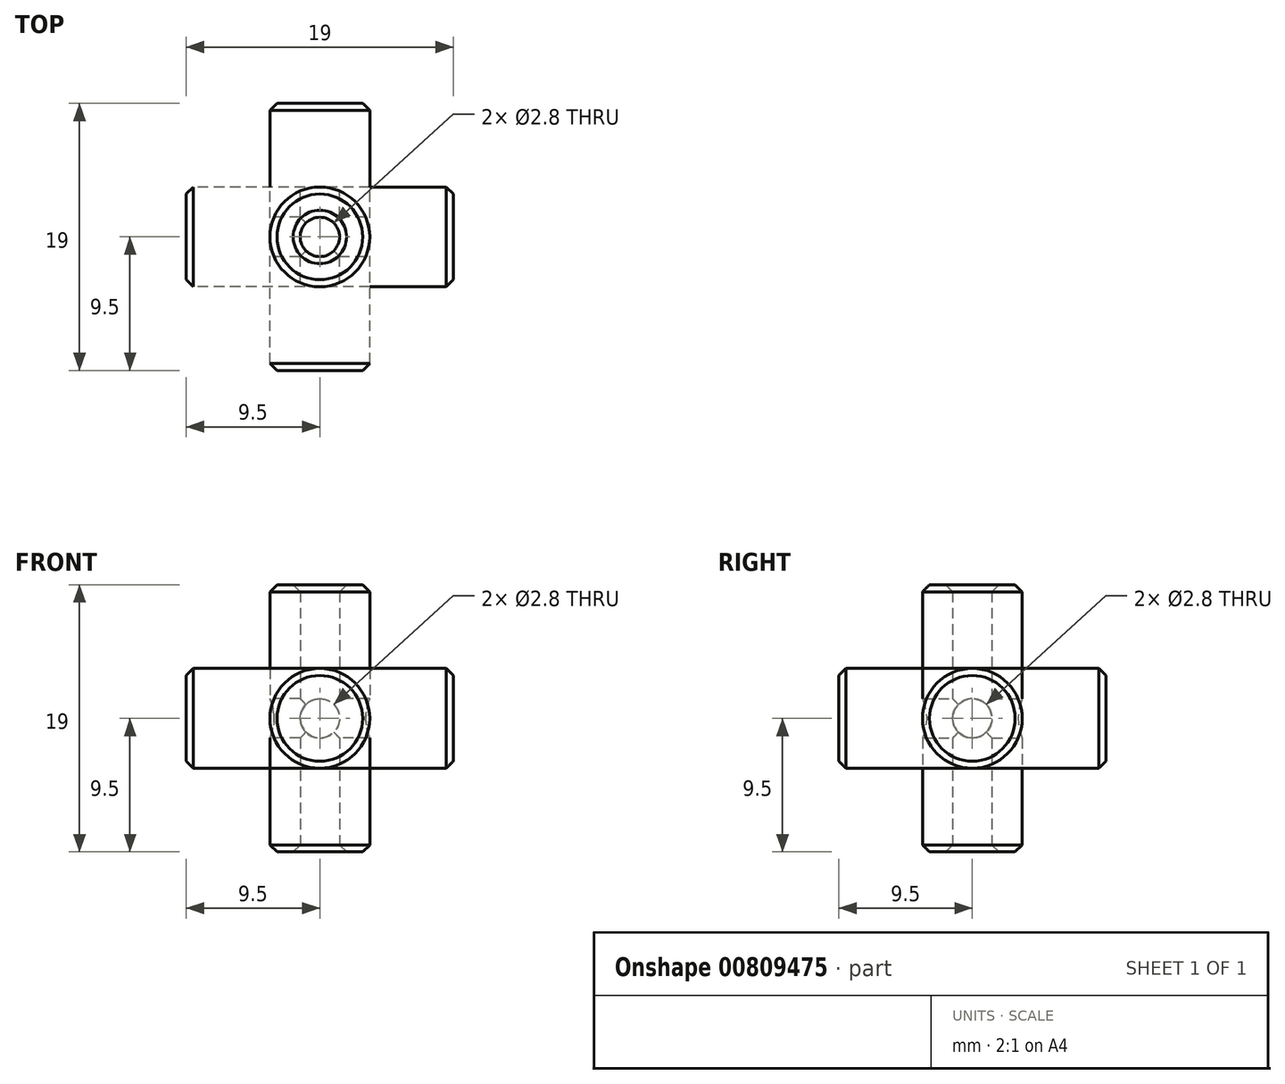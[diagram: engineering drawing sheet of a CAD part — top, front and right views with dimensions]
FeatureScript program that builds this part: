
annotation { "Feature Type Name" : "Feature", "Feature Type Description" : "" }
export const myFeature = defineFeature(function(context is Context, id is Id, definition is map)
    precondition{}
    {
        {
            var Q0;
            Q0=qCreatedBy(makeId("Front.planeOp"),FACE);
            var sketch = newSketch(context, id + "F0", { "sketchPlane" : qUnion([Q0])});
            skCircle(sketch, "E0", {"center": v(0, 0) * mm, "radius": 3.55 * mm});
            skSolve(sketch);
        }
        {
            var Q0;
            Q0=makeQuery(id+"F0.imprint","IMPRINT",FACE,{"disambiguationData":[TD([[makeQuery(id+"F0.imprint","IMPRINT",EDGE,{"derivedFrom":sQuery(id+"F0.wireOp",EDGE,"E0")}),1.0]])]});
            extrude(context, id + "F1", {"entities" : qUnion([Q0]), "endBound" : BoundingType.SYMMETRIC, "depth" : 19 * mm, "offsetDistance" : 25 * mm});
        }
        {
            var Q0;
            Q0=qCreatedBy(makeId("Front.planeOp"),FACE);
            var sketch = newSketch(context, id + "F2", { "sketchPlane" : qUnion([Q0])});
            skCircle(sketch, "E1", {"center": v(0, 0) * mm, "radius": 1.4 * mm});
            skSolve(sketch);
        }
        {
            var Q0;
            Q0 = qSketchRegion(id + "F2", true);
            extrude(context, id + "F3", {"entities" : qUnion([Q0]), "endBound" : BoundingType.SYMMETRIC, "depth" : 20 * mm, "offsetDistance" : 25 * mm});
        }
        {
            var Q0;
            Q0=qCreatedBy(makeId("Front.planeOp"),FACE);
            var sketch = newSketch(context, id + "F4", { "sketchPlane" : qUnion([Q0])});
            skLineSegment(sketch, "E2.bottom", {"start": v(0, 0) * mm, "end": v(10, 0) * mm});
            skLineSegment(sketch, "E2.top", {"start": v(0, 10) * mm, "end": v(10, 10) * mm});
            skLineSegment(sketch, "E2.left", {"start": v(0, 0) * mm, "end": v(0, 10) * mm});
            skLineSegment(sketch, "E2.right", {"start": v(10, 0) * mm, "end": v(10, 10) * mm});
            skSolve(sketch);
        }
        {
            var Q0;
            Q0 = qSketchRegion(id + "F4", true);
            extrude(context, id + "F5", {"entities" : qUnion([Q0]), "depth" : 10 * mm, "offsetDistance" : 25 * mm});
        }
        {
            var Q0;
            Q0=qCreatedBy(makeId("Origin.pointOp"),VERTEX);
            var Q1;
            Q1=makeQuery(id+"F5.opExtrude","CAP_VERTEX",VERTEX,{"disambiguationData":[OSD([sQuery(id+"F4.wireOp",EDGE,"E2.bottom"),sQuery(id+"F4.wireOp",EDGE,"E2.right")])],"isStart":false});
            var Q2;
            Q2=makeQuery(id+"F5.opExtrude","CAP_VERTEX",VERTEX,{"disambiguationData":[OSD([sQuery(id+"F4.wireOp",EDGE,"E2.top"),sQuery(id+"F4.wireOp",EDGE,"E2.right")])],"isStart":false});
            cPlane(context, id + "F6", {"entities" : qUnion([Q0, Q1, Q2]), "cplaneType" : CPlaneType.THREE_POINT, "offset" : 25 * mm, "width" : 150 * mm, "height" : 150 * mm});
        }
        {
            var Q0;
            Q0=qCreatedBy(id+"F6.planeOp",FACE);
            var sketch = newSketch(context, id + "F7", { "sketchPlane" : qUnion([Q0])});
            skLineSegment(sketch, "E3", {"start": v(0, 0) * mm, "end": v(-14.14, 10) * mm});
            skSolve(sketch);
        }
        {
            var Q0;
            Q0=makeQuery(id+"F5.opExtrude","SWEPT_BODY",BODY,{"disambiguationData":[OSD([sQuery(id+"F4.wireOp",EDGE,"E2.bottom"),sQuery(id+"F4.wireOp",EDGE,"E2.top"),sQuery(id+"F4.wireOp",EDGE,"E2.left"),sQuery(id+"F4.wireOp",EDGE,"E2.right")])]});
            deleteBodies(context, id + "F8", {"entities" : qUnion([Q0])});
        }
        {
            var Q0;
            Q0=makeQuery(id+"F3.opExtrude","SWEPT_BODY",BODY,{"disambiguationData":[OSD([sQuery(id+"F2.wireOp",EDGE,"E1")])]});
            var Q1;
            Q1=makeQuery(id+"F1.opExtrude","SWEPT_BODY",BODY,{"disambiguationData":[OSD([sQuery(id+"F0.wireOp",EDGE,"E0")])]});
            var Q2;
            Q2=sQuery(id+"F7.wireOp",EDGE,"E3");
            circularPattern(context, id + "F9", {"entities" : qUnion([Q0, Q1]), "axis" : qUnion([Q2]), "angle" : 360 * degree, "instanceCount" : 3, "equalSpace" : true});
        }
        {
            var Q0;
            Q0=makeQuery(id+"F9.opPattern","COPY",BODY,{"derivedFrom":makeQuery(id+"F3.opExtrude","SWEPT_BODY",BODY,{"disambiguationData":[OSD([sQuery(id+"F2.wireOp",EDGE,"E1")])]}),"instanceName":"2"});
            var Q1;
            Q1=makeQuery(id+"F9.opPattern","COPY",BODY,{"derivedFrom":makeQuery(id+"F3.opExtrude","SWEPT_BODY",BODY,{"disambiguationData":[OSD([sQuery(id+"F2.wireOp",EDGE,"E1")])]}),"instanceName":"1"});
            var Q2;
            Q2=makeQuery(id+"F3.opExtrude","SWEPT_BODY",BODY,{"disambiguationData":[OSD([sQuery(id+"F2.wireOp",EDGE,"E1")])]});
            var Q3;
            Q3=makeQuery(id+"F9.opPattern","COPY",BODY,{"derivedFrom":makeQuery(id+"F1.opExtrude","SWEPT_BODY",BODY,{"disambiguationData":[OSD([sQuery(id+"F0.wireOp",EDGE,"E0")])]}),"instanceName":"2"});
            booleanBodies(context, id + "F10", {"operationType" : BooleanOperationType.SUBTRACTION, "tools" : qUnion([Q0, Q1, Q2]), "targets" : qUnion([Q3])});
        }
        {
            var Q0;
            Q0=makeQuery(id+"F9.opPattern","COPY",FACE,{"derivedFrom":makeQuery(id+"F1.opExtrude","CAP_FACE",FACE,{"disambiguationData":[OSD([sQuery(id+"F0.wireOp",EDGE,"E0")])],"isStart":false}),"instanceName":"2"});
            var Q1;
            Q1=makeQuery(id+"F9.opPattern","COPY",FACE,{"derivedFrom":makeQuery(id+"F1.opExtrude","CAP_FACE",FACE,{"disambiguationData":[OSD([sQuery(id+"F0.wireOp",EDGE,"E0")])],"isStart":true}),"instanceName":"1"});
            var Q2;
            Q2=makeQuery(id+"F9.opPattern","COPY",FACE,{"derivedFrom":makeQuery(id+"F1.opExtrude","CAP_FACE",FACE,{"disambiguationData":[OSD([sQuery(id+"F0.wireOp",EDGE,"E0")])],"isStart":true}),"instanceName":"2"});
            var Q3;
            Q3=makeQuery(id+"F9.opPattern","COPY",FACE,{"derivedFrom":makeQuery(id+"F1.opExtrude","CAP_FACE",FACE,{"disambiguationData":[OSD([sQuery(id+"F0.wireOp",EDGE,"E0")])],"isStart":false}),"instanceName":"1"});
            var Q4;
            Q4=makeQuery(id+"F1.opExtrude","CAP_FACE",FACE,{"disambiguationData":[OSD([sQuery(id+"F0.wireOp",EDGE,"E0")])],"isStart":false});
            var Q5;
            Q5=makeQuery(id+"F1.opExtrude","CAP_FACE",FACE,{"disambiguationData":[OSD([sQuery(id+"F0.wireOp",EDGE,"E0")])],"isStart":true});
            chamfer(context, id + "F11", {"entities" : qUnion([Q0, Q1, Q2, Q3, Q4, Q5]), "width" : 0.5 * mm, "tangentPropagation" : true});
        }
    });
